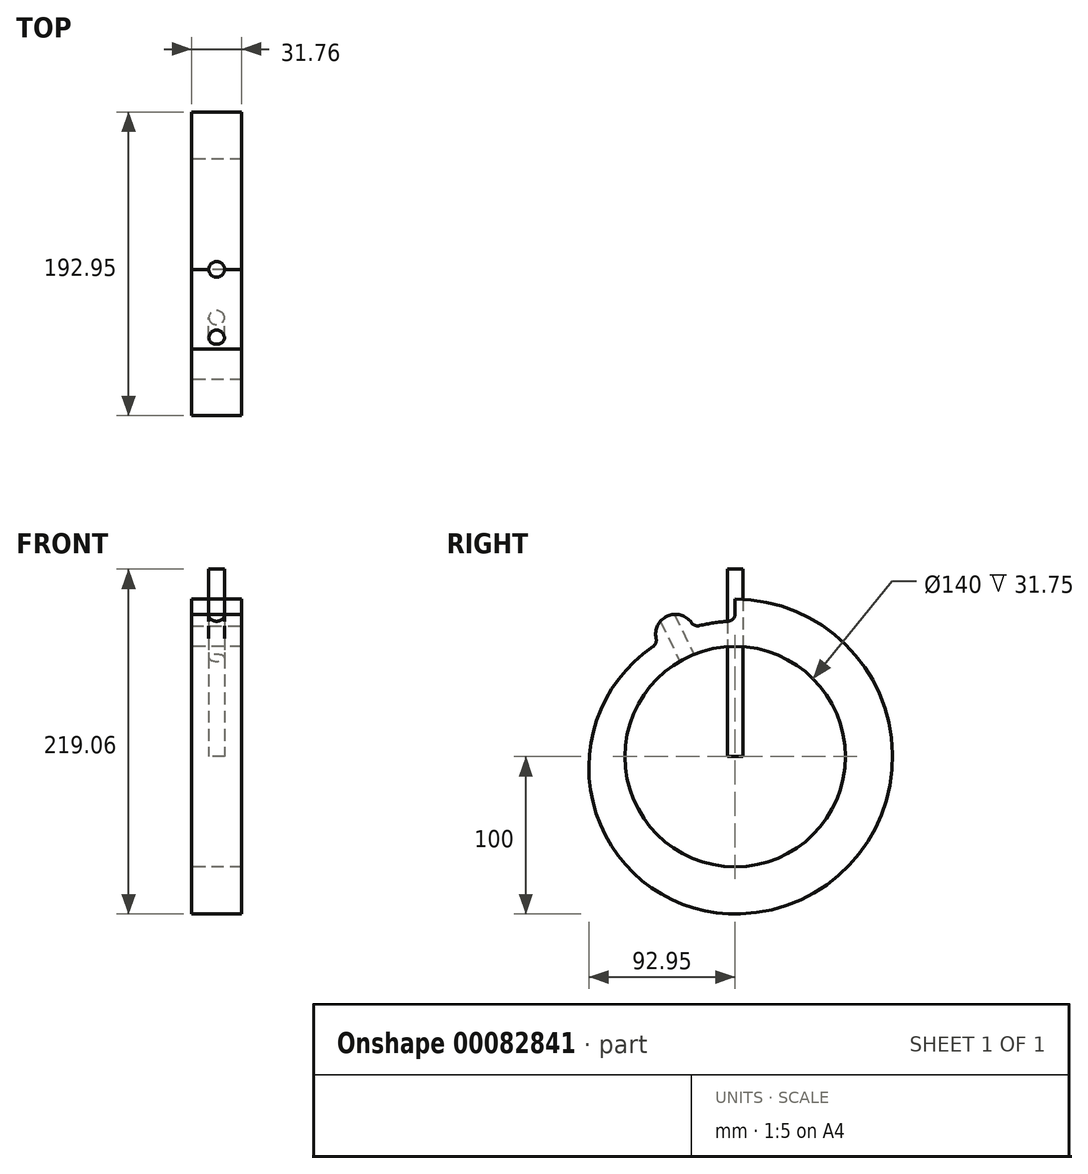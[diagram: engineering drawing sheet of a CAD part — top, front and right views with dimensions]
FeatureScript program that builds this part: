
annotation { "Feature Type Name" : "Feature", "Feature Type Description" : "" }
export const myFeature = defineFeature(function(context is Context, id is Id, definition is map)
    precondition{}
    {
        {
            var Q0;
            Q0=qCreatedBy(makeId("Right.planeOp"),FACE);
            var sketch = newSketch(context, id + "F0", { "sketchPlane" : qUnion([Q0])});
            skCircle(sketch, "E0", {"center": v(0, 0) * mm, "radius": 70 * mm});
            skArc(sketch, "E1", {"start": v(-1.94, -99.98) * mm, "mid": v(100, -0.97) * mm, "end": v(0, 100) * mm});
            skLineSegment(sketch, "E2", {"start": v(0, 107.48) * mm, "end": v(0, 44.89) * mm});
            skLineSegment(sketch, "E3", {"start": v(0, 100) * mm, "end": v(-145.4, 100) * mm, "construction": true});
            skLineSegment(sketch, "E4.0", {"start": v(0.05, 86) * mm, "end": v(-145.4, 86) * mm, "construction": true});
            skArc(sketch, "E5", {"start": v(0.05, 86) * mm, "mid": v(-13.25, 85.04) * mm, "end": v(-26.28, 82.2) * mm});
            skLineSegment(sketch, "E6.0", {"start": v(-38, 107.48) * mm, "end": v(-38, 44.89) * mm, "construction": true});
            skLineSegment(sketch, "E7", {"start": v(0, 0) * mm, "end": v(-38, 77.86) * mm, "construction": true});
            skArc(sketch, "E8", {"start": v(-26.28, 82.2) * mm, "mid": v(-43.11, 89.26) * mm, "end": v(-49.04, 71.99) * mm});
            skArc(sketch, "E9.trimOffspring", {"start": v(-49.04, 71.99) * mm, "mid": v(-88.9, -34.15) * mm, "end": v(3.45, -99.94) * mm});
            skSolve(sketch);
        }
        {
            var Q0;
            Q0 = qSketchRegion(id + "F0", true);
            extrude(context, id + "F1", {"entities" : qUnion([Q0]), "endBound" : BoundingType.SYMMETRIC, "depth" : 31.75 * mm});
        }
        {
            var Q0;
            Q0=makeQuery(id+"F1.opExtrude","SWEPT_EDGE",EDGE,{"disambiguationData":[OSD([sQuery(id+"F0.wireOp",EDGE,"E5"),sQuery(id+"F0.wireOp",EDGE,"E8")])]});
            var Q1;
            Q1=makeQuery(id+"F1.opExtrude","SWEPT_EDGE",EDGE,{"disambiguationData":[OSD([sQuery(id+"F0.wireOp",EDGE,"E8"),sQuery(id+"F0.wireOp",EDGE,"E9.trimOffspring")])]});
            var Q2;
            Q2=makeQuery(id+"F1.opExtrude","SWEPT_EDGE",EDGE,{"disambiguationData":[OSD([sQuery(id+"F0.wireOp",EDGE,"E2"),sQuery(id+"F0.wireOp",EDGE,"E5")])]});
            fillet(context, id + "F2", {"entities" : qUnion([Q0, Q1, Q2]), "radius" : 5 * mm, "tangentPropagation" : true, "allowEdgeOverflow" : false});
        }
        {
            var Q0;
            Q0=qCreatedBy(makeId("Top.planeOp"),FACE);
            var sketch = newSketch(context, id + "F3", { "sketchPlane" : qUnion([Q0])});
            skCircle(sketch, "E10", {"center": v(0, 0) * mm, "radius": 5 * mm});
            skSolve(sketch);
        }
        {
            var Q0;
            Q0=makeQuery(id+"F3.imprint","IMPRINT",FACE,{"disambiguationData":[TD([[makeQuery(id+"F3.imprint","IMPRINT",EDGE,{"derivedFrom":sQuery(id+"F3.wireOp",EDGE,"E10")}),1.0]])]});
            extrude(context, id + "F4", {"entities" : qUnion([Q0]), "depth" : 119.06 * mm});
        }
        {
            var Q0;
            Q0=qCreatedBy(makeId("Top.planeOp"),FACE);
            var sketch = newSketch(context, id + "F5", { "sketchPlane" : qUnion([Q0])});
            skLineSegment(sketch, "E11", {"start": v(-80.7, 0) * mm, "end": v(96.28, 0) * mm, "construction": true});
            skSolve(sketch);
        }
        {
            var Q0;
            Q0=makeQuery(id+"F4.opExtrude","SWEPT_BODY",BODY,{"disambiguationData":[OSD([sQuery(id+"F3.wireOp",EDGE,"E10")])]});
            var Q1;
            Q1=sQuery(id+"F5.wireOp",EDGE,"E11");
            circularPattern(context, id + "F6", {"entities" : qUnion([Q0]), "axis" : qUnion([Q1]), "angle" : 26 * degree, "instanceCount" : 2});
        }
        {
            var Q0;
            Q0=makeQuery(id+"F6.opPattern","COPY",BODY,{"derivedFrom":makeQuery(id+"F4.opExtrude","SWEPT_BODY",BODY,{"disambiguationData":[OSD([sQuery(id+"F3.wireOp",EDGE,"E10")])]}),"instanceName":"1"});
            var Q1;
            Q1=makeQuery(id+"F1.opExtrude","SWEPT_BODY",BODY,{"disambiguationData":[OSD([sQuery(id+"F0.wireOp",EDGE,"E0"),sQuery(id+"F0.wireOp",EDGE,"E1"),sQuery(id+"F0.wireOp",EDGE,"E2"),sQuery(id+"F0.wireOp",EDGE,"E5"),sQuery(id+"F0.wireOp",EDGE,"E8"),sQuery(id+"F0.wireOp",EDGE,"E9.trimOffspring")])]});
            booleanBodies(context, id + "F7", {"operationType" : BooleanOperationType.SUBTRACTION, "tools" : qUnion([Q0]), "targets" : qUnion([Q1])});
        }
    });
